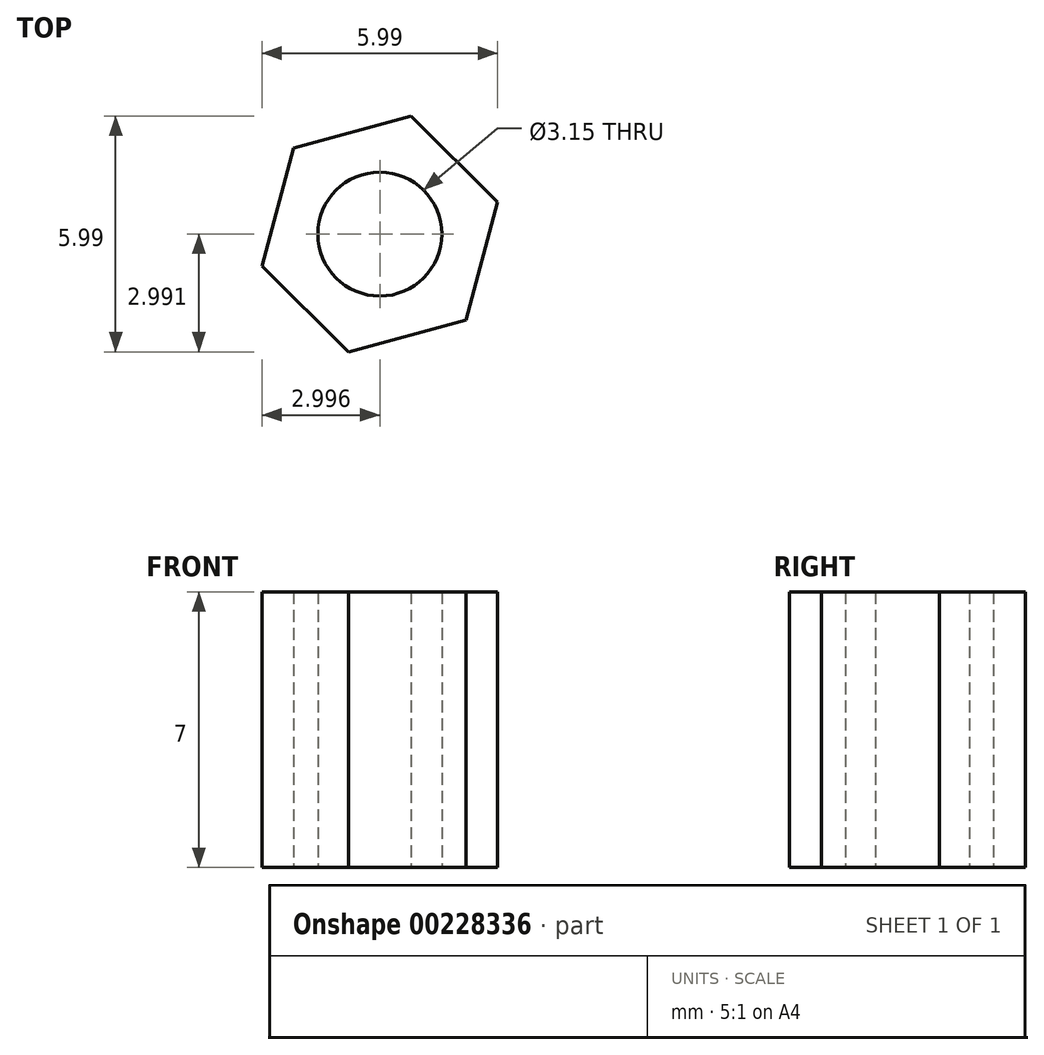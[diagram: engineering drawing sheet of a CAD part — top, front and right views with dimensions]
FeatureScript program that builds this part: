
annotation { "Feature Type Name" : "Feature", "Feature Type Description" : "" }
export const myFeature = defineFeature(function(context is Context, id is Id, definition is map)
    precondition{}
    {
        {
            var Q0;
            Q0=qCreatedBy(makeId("Top.planeOp"),FACE);
            var sketch = newSketch(context, id + "F0", { "sketchPlane" : qUnion([Q0])});
            skCircle(sketch, "E0", {"center": v(-3.03, 13.06) * mm, "radius": 1.57 * mm});
            skCircle(sketch, "E1.cCircle", {"center": v(-3.03, 13.06) * mm, "radius": 3.1 * mm, "construction": true});
            skLineSegment(sketch, "E1.0", {"start": v(-6.03, 12.25) * mm, "end": v(-5.23, 15.25) * mm});
            skLineSegment(sketch, "E1.1", {"start": v(-5.23, 15.25) * mm, "end": v(-2.24, 16.06) * mm});
            skLineSegment(sketch, "E1.2", {"start": v(-2.24, 16.06) * mm, "end": v(-0.04, 13.87) * mm});
            skLineSegment(sketch, "E1.3", {"start": v(-0.04, 13.87) * mm, "end": v(-0.84, 10.87) * mm});
            skLineSegment(sketch, "E1.4", {"start": v(-0.84, 10.87) * mm, "end": v(-3.83, 10.07) * mm});
            skLineSegment(sketch, "E1.5", {"start": v(-3.83, 10.07) * mm, "end": v(-6.03, 12.25) * mm});
            skSolve(sketch);
        }
        {
            var Q0;
            Q0 = qSketchRegion(id + "F0", true);
            extrude(context, id + "F1", {"entities" : qUnion([Q0]), "depth" : 7 * mm});
        }
    });
